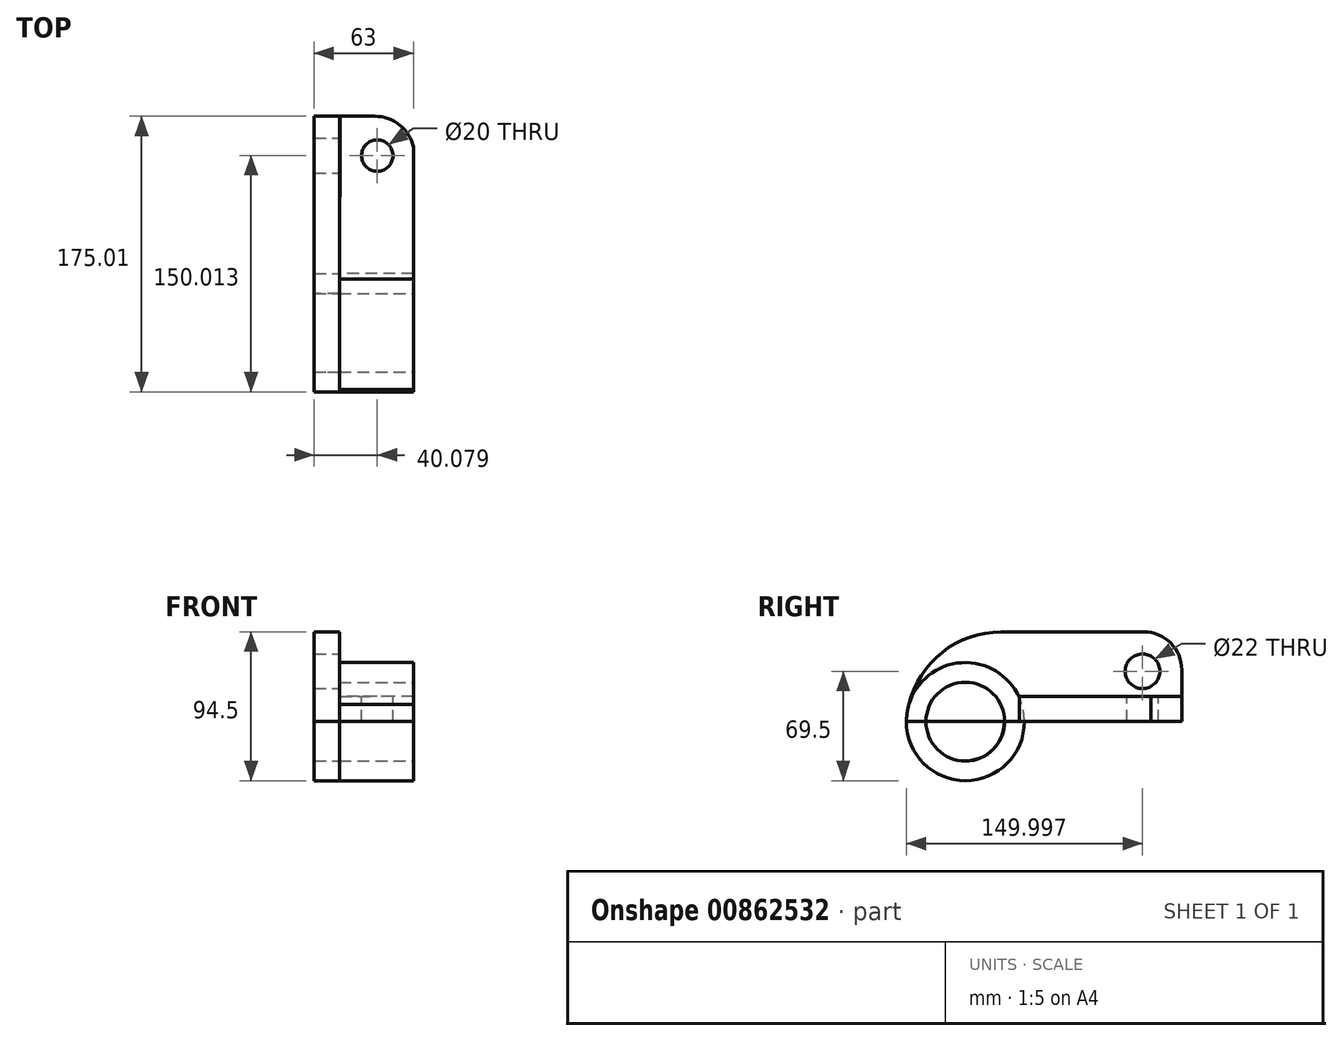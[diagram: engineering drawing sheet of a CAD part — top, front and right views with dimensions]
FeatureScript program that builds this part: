
annotation { "Feature Type Name" : "Feature", "Feature Type Description" : "" }
export const myFeature = defineFeature(function(context is Context, id is Id, definition is map)
    precondition{}
    {
        {
            var Q0;
            Q0=qCreatedBy(makeId("Right.planeOp"),FACE);
            var sketch = newSketch(context, id + "F0", { "sketchPlane" : qUnion([Q0])});
            skLineSegment(sketch, "E0", {"start": v(-75.05, 0) * mm, "end": v(99.95, 0) * mm});
            skLineSegment(sketch, "E1", {"start": v(99.95, 0) * mm, "end": v(99.95, 57) * mm});
            skLineSegment(sketch, "E2", {"start": v(99.95, 57) * mm, "end": v(-75.05, 57) * mm});
            skLineSegment(sketch, "E3", {"start": v(-75.05, 57) * mm, "end": v(-75.05, 0) * mm});
            skSolve(sketch);
        }
        {
            var Q0;
            Q0=makeQuery(id+"F0.imprint","IMPRINT",FACE,{"disambiguationData":[TD([[makeQuery(id+"F0.imprint","IMPRINT",EDGE,{"derivedFrom":sQuery(id+"F0.wireOp",EDGE,"E0")}),1.0]])]});
            extrude(context, id + "F1", {"entities" : qUnion([Q0]), "depth" : 16 * mm, "offsetDistance" : 25 * mm});
        }
        {
            var Q0;
            Q0=makeQuery(id+"F1.opExtrude","CAP_FACE",FACE,{"disambiguationData":[OSD([sQuery(id+"F0.wireOp",EDGE,"E0"),sQuery(id+"F0.wireOp",EDGE,"E1"),sQuery(id+"F0.wireOp",EDGE,"E2"),sQuery(id+"F0.wireOp",EDGE,"E3")])],"isStart":false});
            var sketch = newSketch(context, id + "F2", { "sketchPlane" : qUnion([Q0])});
            skLineSegment(sketch, "E4", {"start": v(99.95, 0) * mm, "end": v(74.95, 0) * mm});
            skLineSegment(sketch, "E5", {"start": v(74.95, 0) * mm, "end": v(74.95, 32) * mm});
            skCircle(sketch, "E6", {"center": v(74.95, 32) * mm, "radius": 11 * mm});
            skSolve(sketch);
        }
        {
            var Q0;
            Q0=makeQuery(id+"F2.imprint","IMPRINT",FACE,{"disambiguationData":[TD([[makeQuery(id+"F2.imprint","IMPRINT",EDGE,{"derivedFrom":sQuery(id+"F2.wireOp",EDGE,"E6")}),1.0]])]});
            extrude(context, id + "F3", {"entities" : qUnion([Q0]), "operationType" : NewBodyOperationType.REMOVE, "oppositeDirection" : true, "depth" : 62 * mm, "offsetDistance" : 25 * mm});
        }
        {
            var Q0;
            Q0=makeQuery(id+"F1.opExtrude","SWEPT_EDGE",EDGE,{"disambiguationData":[OSD([sQuery(id+"F0.wireOp",EDGE,"E1"),sQuery(id+"F0.wireOp",EDGE,"E2")])]});
            fillet(context, id + "F4", {"entities" : qUnion([Q0]), "radius" : 24.14 * mm, "tangentPropagation" : true, "allowEdgeOverflow" : false});
        }
        {
            var Q0;
            Q0=makeQuery(id+"F1.opExtrude","SWEPT_EDGE",EDGE,{"disambiguationData":[OSD([sQuery(id+"F0.wireOp",EDGE,"E2"),sQuery(id+"F0.wireOp",EDGE,"E3")])]});
            fillet(context, id + "F5", {"entities" : qUnion([Q0]), "radius" : 60.36 * mm, "tangentPropagation" : true, "allowEdgeOverflow" : false});
        }
        {
            var Q0;
            Q0=makeQuery(id+"F1.opExtrude","CAP_FACE",FACE,{"disambiguationData":[OSD([sQuery(id+"F0.wireOp",EDGE,"E0"),sQuery(id+"F0.wireOp",EDGE,"E1"),sQuery(id+"F0.wireOp",EDGE,"E2"),sQuery(id+"F0.wireOp",EDGE,"E3")])],"isStart":false});
            var sketch = newSketch(context, id + "F6", { "sketchPlane" : qUnion([Q0])});
            skLineSegment(sketch, "E7", {"start": v(-75.05, 0) * mm, "end": v(-37.55, 0) * mm});
            skCircle(sketch, "E8", {"center": v(-37.55, 0) * mm, "radius": 37.5 * mm});
            skSolve(sketch);
        }
        {
            var Q0;
            {var subQ0=sQuery(id+"F6.wireOp",EDGE,"E7");Q0=makeQuery(id+"F6.imprint","IMPRINT",FACE,{"disambiguationData":[TD([[makeQuery(id+"F6.imprint","IMPRINT",EDGE,{"derivedFrom":subQ0}),-1.0]])]});}
            extrude(context, id + "F7", {"entities" : qUnion([Q0]), "depth" : 47 * mm, "offsetDistance" : 25 * mm});
        }
        {
            var Q0;
            Q0=makeQuery(id+"F1.opExtrude","CAP_FACE",FACE,{"disambiguationData":[OSD([sQuery(id+"F0.wireOp",EDGE,"E0"),sQuery(id+"F0.wireOp",EDGE,"E1"),sQuery(id+"F0.wireOp",EDGE,"E2"),sQuery(id+"F0.wireOp",EDGE,"E3")])],"isStart":false});
            var sketch = newSketch(context, id + "F8", { "sketchPlane" : qUnion([Q0])});
            skLineSegment(sketch, "E9", {"start": v(-75.05, 0) * mm, "end": v(-37.55, 0) * mm});
            skCircle(sketch, "E10", {"center": v(-37.55, 0) * mm, "radius": 37.5 * mm});
            skSolve(sketch);
        }
        {
            var Q0;
            {var subQ0=sQuery(id+"F8.wireOp",EDGE,"E9");Q0=makeQuery(id+"F8.imprint","IMPRINT",FACE,{"disambiguationData":[TD([[makeQuery(id+"F8.imprint","IMPRINT",EDGE,{"derivedFrom":subQ0}),1.0]])]});}
            extrude(context, id + "F9", {"entities" : qUnion([Q0]), "depth" : 47 * mm, "offsetDistance" : 25 * mm});
        }
        {
            var Q0;
            Q0=makeQuery(id+"F9.opExtrude","CAP_FACE",FACE,{"disambiguationData":[OSD([sQuery(id+"F0.wireOp",EDGE,"E0"),sQuery(id+"F0.wireOp",EDGE,"E1"),sQuery(id+"F0.wireOp",EDGE,"E2"),sQuery(id+"F0.wireOp",EDGE,"E3"),sQuery(id+"F8.wireOp",EDGE,"E9"),sQuery(id+"F8.wireOp",EDGE,"E10")])],"isStart":false});
            var sketch = newSketch(context, id + "F10", { "sketchPlane" : qUnion([Q0])});
            skLineSegment(sketch, "E11", {"start": v(-75.05, 0) * mm, "end": v(-37.55, 0) * mm});
            skCircle(sketch, "E12", {"center": v(-37.55, 0) * mm, "radius": 25 * mm});
            skSolve(sketch);
        }
        {
            var Q0;
            {var subQ0=sQuery(id+"F10.wireOp",EDGE,"E11");var subQ3=sQuery(id+"F10.wireOp",EDGE,"E12");var subQ4=makeQuery(id+"F10.imprint","INTERSECT",VERTEX,{"derivedFrom":[subQ0,subQ3]});Q0=makeQuery(id+"F10.imprint","IMPRINT",FACE,{"disambiguationData":[TD([[makeQuery(id+"F10.imprint","IMPRINT",EDGE,{"disambiguationData":[TD([[subQ4,-1.0]])],"derivedFrom":subQ0}),1.0]])]});}
            extrude(context, id + "F11", {"entities" : qUnion([Q0]), "operationType" : NewBodyOperationType.REMOVE, "oppositeDirection" : true, "depth" : 47 * mm, "offsetDistance" : 25 * mm});
        }
        {
            var Q0;
            Q0=makeQuery(id+"F7.opExtrude","CAP_FACE",FACE,{"disambiguationData":[OSD([sQuery(id+"F0.wireOp",EDGE,"E0"),sQuery(id+"F6.wireOp",EDGE,"E7"),sQuery(id+"F6.wireOp",EDGE,"E8")])],"isStart":false});
            var sketch = newSketch(context, id + "F12", { "sketchPlane" : qUnion([Q0])});
            skLineSegment(sketch, "E13", {"start": v(-75.05, 0) * mm, "end": v(-37.55, 0) * mm});
            skCircle(sketch, "E14", {"center": v(-37.55, 0) * mm, "radius": 25 * mm});
            skSolve(sketch);
        }
        {
            var Q0;
            {var subQ0=sQuery(id+"F12.wireOp",EDGE,"E13");var subQ3=sQuery(id+"F12.wireOp",EDGE,"E14");var subQ4=makeQuery(id+"F12.imprint","INTERSECT",VERTEX,{"derivedFrom":[subQ0,subQ3]});Q0=makeQuery(id+"F12.imprint","IMPRINT",FACE,{"disambiguationData":[TD([[makeQuery(id+"F12.imprint","IMPRINT",EDGE,{"disambiguationData":[TD([[subQ4,-1.0]])],"derivedFrom":subQ0}),-1.0]])]});}
            extrude(context, id + "F13", {"entities" : qUnion([Q0]), "operationType" : NewBodyOperationType.REMOVE, "oppositeDirection" : true, "depth" : 47 * mm, "offsetDistance" : 25 * mm});
        }
        {
            var Q0;
            Q0=makeQuery(id+"F7.opExtrude","CAP_FACE",FACE,{"disambiguationData":[OSD([sQuery(id+"F0.wireOp",EDGE,"E0"),sQuery(id+"F6.wireOp",EDGE,"E7"),sQuery(id+"F6.wireOp",EDGE,"E8")])],"isStart":true});
            var sketch = newSketch(context, id + "F14", { "sketchPlane" : qUnion([Q0])});
            skLineSegment(sketch, "E15", {"start": v(75.05, 0) * mm, "end": v(37.55, 0) * mm});
            skCircle(sketch, "E16", {"center": v(37.55, 0) * mm, "radius": 37.5 * mm});
            skSolve(sketch);
        }
        {
            var Q0;
            {var subQ0=sQuery(id+"F14.wireOp",EDGE,"E16");Q0=makeQuery(id+"F14.imprint","IMPRINT",FACE,{"disambiguationData":[TD([[makeQuery(id+"F14.imprint","IMPRINT",EDGE,{"disambiguationData":[OD(1.0)],"derivedFrom":subQ0}),-1.0]])]});}
            extrude(context, id + "F15", {"entities" : qUnion([Q0]), "depth" : 16 * mm, "offsetDistance" : 25 * mm});
        }
        {
            var Q0;
            Q0=makeQuery(id+"F1.opExtrude","CAP_FACE",FACE,{"disambiguationData":[OSD([sQuery(id+"F0.wireOp",EDGE,"E0"),sQuery(id+"F0.wireOp",EDGE,"E1"),sQuery(id+"F0.wireOp",EDGE,"E2"),sQuery(id+"F0.wireOp",EDGE,"E3")])],"isStart":true});
            var sketch = newSketch(context, id + "F16", { "sketchPlane" : qUnion([Q0])});
            skLineSegment(sketch, "E17", {"start": v(75.05, 0) * mm, "end": v(37.74, 0) * mm});
            skCircle(sketch, "E18", {"center": v(37.74, 0) * mm, "radius": 25 * mm});
            skSolve(sketch);
        }
        {
            var Q0;
            {var subQ0=sQuery(id+"F16.wireOp",EDGE,"E17");var subQ1=makeQuery(id+"F1.opExtrude","CAP_EDGE",EDGE,{"disambiguationData":[OSD([sQuery(id+"F0.wireOp",EDGE,"E0")])],"isStart":true});var subQ2=makeQuery(id+"F16.imprint","INTERSECT",VERTEX,{"derivedFrom":[subQ1,subQ0]});Q0=makeQuery(id+"F16.imprint","IMPRINT",FACE,{"disambiguationData":[TD([[makeQuery(id+"F16.imprint","IMPRINT",EDGE,{"disambiguationData":[TD([[subQ2,1.0]])],"derivedFrom":subQ0}),1.0]])]});}
            extrude(context, id + "F17", {"entities" : qUnion([Q0]), "oppositeDirection" : true, "depth" : 16 * mm, "offsetDistance" : 25 * mm});
        }
        {
            var Q0;
            Q0=qCreatedBy(makeId("Top.planeOp"),FACE);
            var sketch = newSketch(context, id + "F18", { "sketchPlane" : qUnion([Q0])});
            skLineSegment(sketch, "E19", {"start": v(16.58, 99.96) * mm, "end": v(63.58, 99.96) * mm});
            skLineSegment(sketch, "E20", {"start": v(63.58, 99.96) * mm, "end": v(63.58, -3.3) * mm});
            skLineSegment(sketch, "E21", {"start": v(63.58, -3.3) * mm, "end": v(16.18, -3.3) * mm});
            skLineSegment(sketch, "E22", {"start": v(16.18, -3.3) * mm, "end": v(16.58, 99.96) * mm});
            skSolve(sketch);
        }
        {
            var Q0;
            Q0=makeQuery(id+"F18.imprint","IMPRINT",FACE,{"disambiguationData":[TD([[makeQuery(id+"F18.imprint","IMPRINT",EDGE,{"derivedFrom":sQuery(id+"F18.wireOp",EDGE,"E19")}),-1.0]])]});
            extrude(context, id + "F19", {"entities" : qUnion([Q0]), "depth" : 16 * mm, "offsetDistance" : 25 * mm});
        }
        {
            var Q0;
            Q0=makeQuery(id+"F19.opExtrude","CAP_FACE",FACE,{"disambiguationData":[OSD([sQuery(id+"F18.wireOp",EDGE,"E19"),sQuery(id+"F18.wireOp",EDGE,"E20"),sQuery(id+"F18.wireOp",EDGE,"E21"),sQuery(id+"F18.wireOp",EDGE,"E22")])],"isStart":false});
            var sketch = newSketch(context, id + "F20", { "sketchPlane" : qUnion([Q0])});
            skLineSegment(sketch, "E23", {"start": v(16.58, 99.96) * mm, "end": v(40.08, 99.96) * mm});
            skLineSegment(sketch, "E24", {"start": v(40.08, 99.96) * mm, "end": v(40.08, 74.96) * mm});
            skCircle(sketch, "E25", {"center": v(40.08, 74.96) * mm, "radius": 10 * mm});
            skSolve(sketch);
        }
        {
            var Q0;
            Q0=makeQuery(id+"F20.imprint","IMPRINT",FACE,{"disambiguationData":[TD([[makeQuery(id+"F20.imprint","IMPRINT",EDGE,{"derivedFrom":sQuery(id+"F20.wireOp",EDGE,"E25")}),1.0]])]});
            extrude(context, id + "F21", {"entities" : qUnion([Q0]), "operationType" : NewBodyOperationType.REMOVE, "oppositeDirection" : true, "depth" : 25 * mm, "offsetDistance" : 25 * mm});
        }
        {
            var Q0;
            Q0=makeQuery(id+"F19.opExtrude","SWEPT_EDGE",EDGE,{"disambiguationData":[OSD([sQuery(id+"F18.wireOp",EDGE,"E19"),sQuery(id+"F18.wireOp",EDGE,"E20")])]});
            fillet(context, id + "F22", {"entities" : qUnion([Q0]), "radius" : 25 * mm, "tangentPropagation" : true, "allowEdgeOverflow" : false});
        }
        {
            var Q0;
            Q0=makeQuery(id+"F19.opExtrude","SWEPT_FACE",FACE,{"disambiguationData":[OSD([sQuery(id+"F18.wireOp",EDGE,"E21")])]});
            var sketch = newSketch(context, id + "F23", { "sketchPlane" : qUnion([Q0])});
            skLineSegment(sketch, "E26.bottom", {"start": v(63, 0) * mm, "end": v(63.58, 0) * mm});
            skLineSegment(sketch, "E26.top", {"start": v(63, 16) * mm, "end": v(63.58, 16) * mm});
            skLineSegment(sketch, "E26.left", {"start": v(63, 0) * mm, "end": v(63, 16) * mm});
            skLineSegment(sketch, "E26.right", {"start": v(63.58, 0) * mm, "end": v(63.58, 16) * mm});
            skSolve(sketch);
        }
        {
            var Q0;
            Q0=makeQuery(id+"F23.imprint","IMPRINT",FACE,{"disambiguationData":[TD([[makeQuery(id+"F23.imprint","IMPRINT",EDGE,{"derivedFrom":sQuery(id+"F23.wireOp",EDGE,"E26.bottom")}),-1.0]])]});
            extrude(context, id + "F24", {"entities" : qUnion([Q0]), "operationType" : NewBodyOperationType.REMOVE, "oppositeDirection" : true, "depth" : 126 * mm, "offsetDistance" : 25 * mm});
        }
    });
